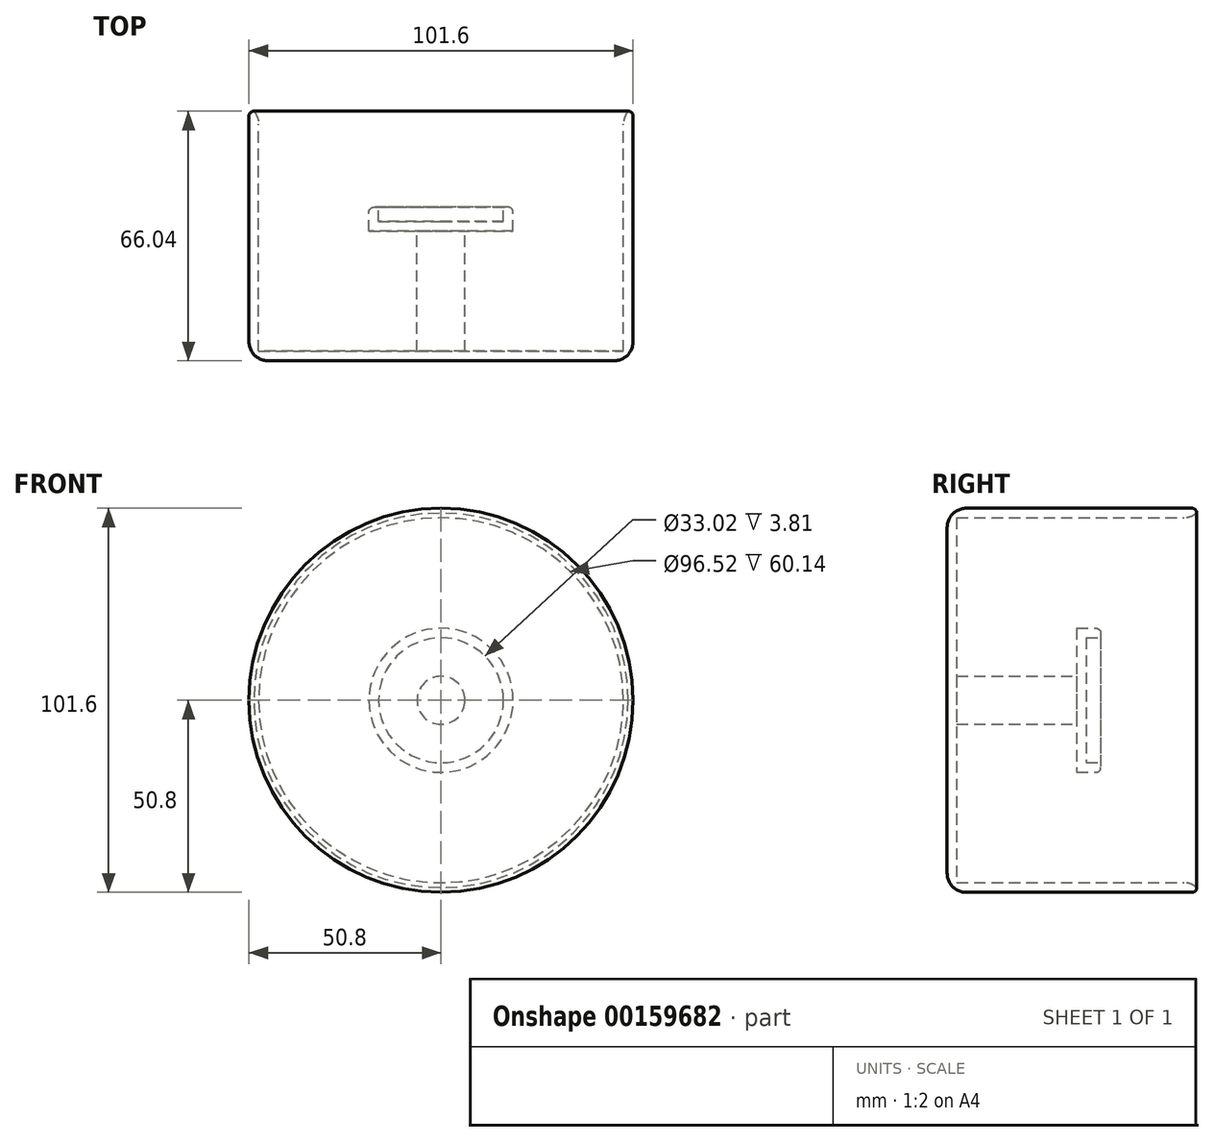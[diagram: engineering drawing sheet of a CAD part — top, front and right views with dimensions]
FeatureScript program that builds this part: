
annotation { "Feature Type Name" : "Feature", "Feature Type Description" : "" }
export const myFeature = defineFeature(function(context is Context, id is Id, definition is map)
    precondition{}
    {
        {
            var Q0;
            Q0=qCreatedBy(makeId("Top.planeOp"),FACE);
            var sketch = newSketch(context, id + "F0", { "sketchPlane" : qUnion([Q0])});
            skLineSegment(sketch, "E0", {"start": v(0, 0) * mm, "end": v(48.26, 0) * mm});
            skLineSegment(sketch, "E1", {"start": v(48.26, 0) * mm, "end": v(48.26, 63.5) * mm});
            skLineSegment(sketch, "E2", {"start": v(6.35, 0) * mm, "end": v(6.35, 31.75) * mm});
            skLineSegment(sketch, "E3", {"start": v(6.35, 31.75) * mm, "end": v(19.05, 31.75) * mm});
            skLineSegment(sketch, "E4", {"start": v(19.05, 31.75) * mm, "end": v(19.05, 38.1) * mm});
            skLineSegment(sketch, "E5.0", {"start": v(16.51, 34.3) * mm, "end": v(16.51, 38.1) * mm});
            skLineSegment(sketch, "E5.1", {"start": v(0, 34.3) * mm, "end": v(16.51, 34.3) * mm});
            skLineSegment(sketch, "E6.0", {"start": v(50.8, -2.54) * mm, "end": v(50.8, 63.5) * mm});
            skLineSegment(sketch, "E6.1", {"start": v(0, -2.54) * mm, "end": v(50.8, -2.54) * mm});
            skLineSegment(sketch, "E7", {"start": v(48.26, 63.5) * mm, "end": v(50.8, 63.5) * mm});
            skLineSegment(sketch, "E8", {"start": v(16.51, 38.1) * mm, "end": v(19.05, 38.1) * mm});
            skLineSegment(sketch, "E9", {"start": v(0, 34.3) * mm, "end": v(0, 34.3) * mm});
            skLineSegment(sketch, "E10", {"start": v(0, 34.3) * mm, "end": v(0, -2.54) * mm});
            skSolve(sketch);
        }
        {
            var Q0;
            {var subQ0=sQuery(id+"F0.wireOp",EDGE,"E1");Q0=makeQuery(id+"F0.imprint","IMPRINT",FACE,{"disambiguationData":[TD([[makeQuery(id+"F0.imprint","IMPRINT",EDGE,{"derivedFrom":subQ0}),-1.0]])]});}
            var Q1;
            {var subQ4=sQuery(id+"F0.wireOp",EDGE,"E2");Q1=makeQuery(id+"F0.imprint","IMPRINT",FACE,{"disambiguationData":[TD([[makeQuery(id+"F0.imprint","IMPRINT",EDGE,{"derivedFrom":subQ4}),1.0]])]});}
            var Q2;
            Q2=sQuery(id+"F0.wireOp",EDGE,"E10");
            revolve(context, id + "F1", {"entities" : qUnion([Q0, Q1]), "axis" : qUnion([Q2]), "revolveType" : RevolveType.FULL});
        }
        {
            var Q0;
            Q0=makeQuery(id+"F1.opRevolve","SWEPT_EDGE",EDGE,{"disambiguationData":[OSD([sQuery(id+"F0.wireOp",EDGE,"E6.0"),sQuery(id+"F0.wireOp",EDGE,"E6.1")])]});
            fillet(context, id + "F2", {"entities" : qUnion([Q0]), "radius" : 5.08 * mm, "tangentPropagation" : true, "allowEdgeOverflow" : false});
        }
        {
            var Q0;
            Q0=makeQuery(id+"F1.opRevolve","SWEPT_EDGE",EDGE,{"disambiguationData":[OSD([sQuery(id+"F0.wireOp",EDGE,"E6.0"),sQuery(id+"F0.wireOp",EDGE,"E7")])]});
            fillet(context, id + "F3", {"entities" : qUnion([Q0]), "radius" : 1.27 * mm, "tangentPropagation" : true, "allowEdgeOverflow" : false});
        }
        {
            var Q0;
            Q0=makeQuery(id+"F1.opRevolve","SWEPT_EDGE",EDGE,{"disambiguationData":[OSD([sQuery(id+"F0.wireOp",EDGE,"E1"),sQuery(id+"F0.wireOp",EDGE,"E7")])]});
            fillet(context, id + "F4", {"entities" : qUnion([Q0]), "radius" : 5.08 * mm, "tangentPropagation" : true, "allowEdgeOverflow" : false});
        }
        {
            var Q0;
            Q0=makeQuery(id+"F1.opRevolve","SWEPT_EDGE",EDGE,{"disambiguationData":[OSD([sQuery(id+"F0.wireOp",EDGE,"E4"),sQuery(id+"F0.wireOp",EDGE,"E8")])]});
            fillet(context, id + "F5", {"entities" : qUnion([Q0]), "radius" : 1.27 * mm, "tangentPropagation" : true, "allowEdgeOverflow" : false});
        }
    });
